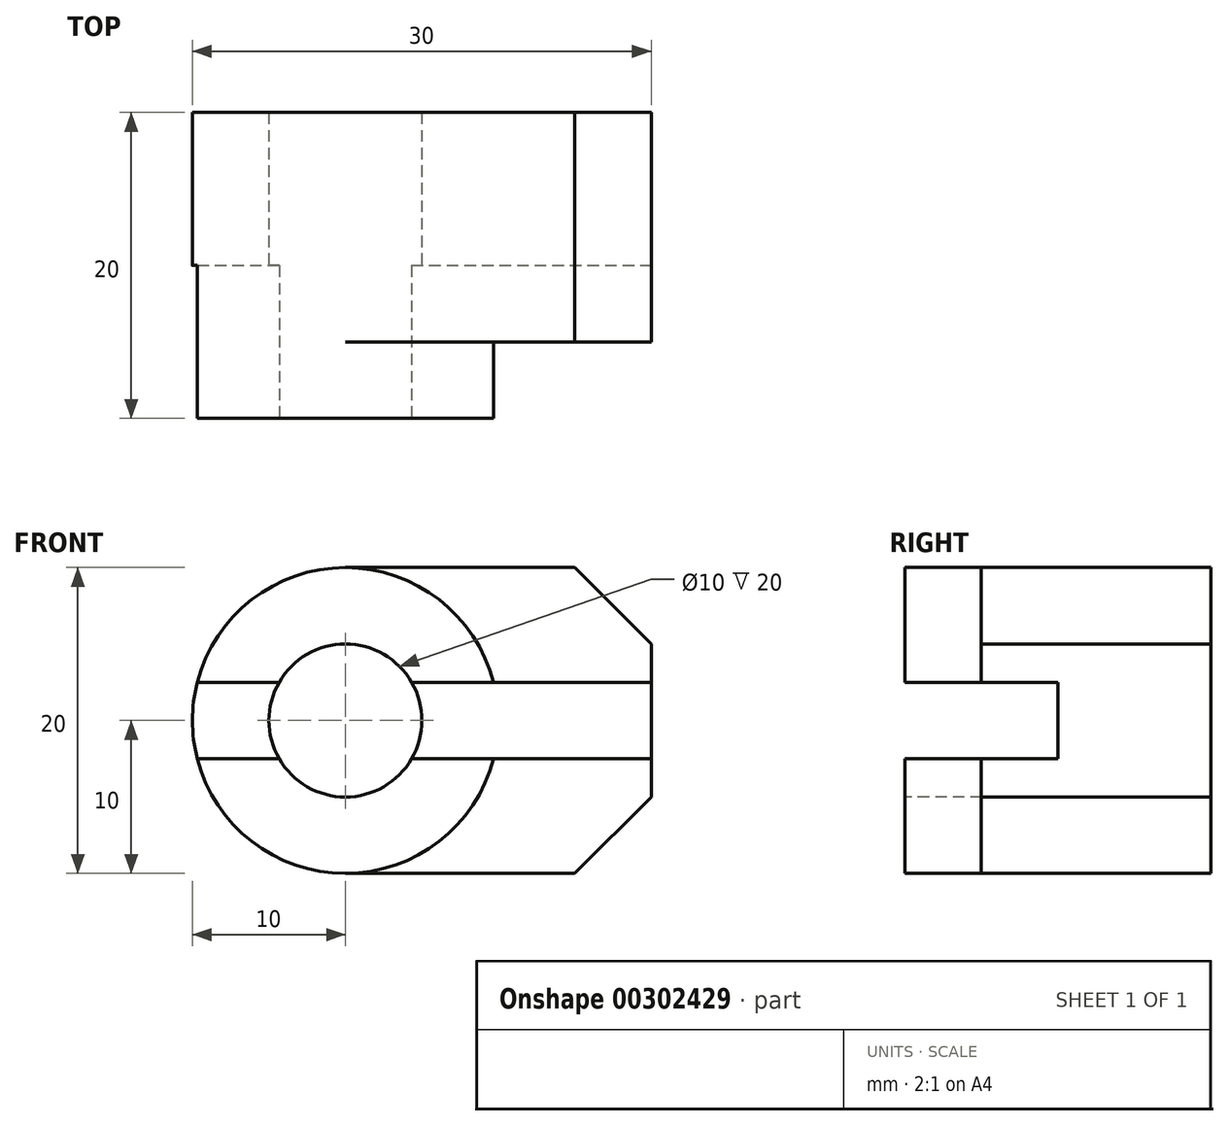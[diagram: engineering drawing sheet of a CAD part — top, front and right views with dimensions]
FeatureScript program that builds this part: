
annotation { "Feature Type Name" : "Feature", "Feature Type Description" : "" }
export const myFeature = defineFeature(function(context is Context, id is Id, definition is map)
    precondition{}
    {
        {
            var Q0;
            Q0=qCreatedBy(makeId("Front.planeOp"),FACE);
            var sketch = newSketch(context, id + "F0", { "sketchPlane" : qUnion([Q0])});
            skCircle(sketch, "E0", {"center": v(0, 0) * mm, "radius": 10 * mm});
            skSolve(sketch);
        }
        {
            var Q0;
            Q0 = qSketchRegion(id + "F0", true);
            extrude(context, id + "F1", {"entities" : qUnion([Q0]), "depth" : 20 * mm});
        }
        {
            var Q0;
            Q0=qCreatedBy(makeId("Front.planeOp"),FACE);
            var sketch = newSketch(context, id + "F2", { "sketchPlane" : qUnion([Q0])});
            skArc(sketch, "E1", {"start": v(10, 0) * mm, "mid": v(7.07, 7.07) * mm, "end": v(0, 10) * mm});
            skLineSegment(sketch, "E2", {"start": v(0, 10) * mm, "end": v(15, 10) * mm});
            skLineSegment(sketch, "E3", {"start": v(15, 10) * mm, "end": v(20, 5) * mm});
            skLineSegment(sketch, "E4", {"start": v(20, 5) * mm, "end": v(20, 0) * mm});
            skLineSegment(sketch, "E5.MirrorCS", {"start": v(0, -10) * mm, "end": v(15, -10) * mm});
            skLineSegment(sketch, "E6.MirrorCS", {"start": v(15, -10) * mm, "end": v(20, -5) * mm});
            skLineSegment(sketch, "E7.MirrorCS", {"start": v(20, -5) * mm, "end": v(20, 0) * mm});
            skArc(sketch, "E8.MirrorCS", {"start": v(10, 0) * mm, "mid": v(7.07, -7.07) * mm, "end": v(0, -10) * mm});
            skSolve(sketch);
        }
        {
            var Q0;
            Q0 = qSketchRegion(id + "F2", true);
            extrude(context, id + "F3", {"entities" : qUnion([Q0]), "operationType" : NewBodyOperationType.ADD, "depth" : 15 * mm});
        }
        {
            var Q0;
            Q0=makeQuery(id+"F1.opExtrude","CAP_FACE",FACE,{"disambiguationData":[OSD([sQuery(id+"F0.wireOp",EDGE,"E0")])],"isStart":false});
            var sketch = newSketch(context, id + "F4", { "sketchPlane" : qUnion([Q0])});
            skCircle(sketch, "E9", {"center": v(0, 0) * mm, "radius": 5 * mm});
            skSolve(sketch);
        }
        {
            var Q0;
            Q0 = qSketchRegion(id + "F4", true);
            extrude(context, id + "F5", {"entities" : qUnion([Q0]), "operationType" : NewBodyOperationType.REMOVE, "endBound" : BoundingType.THROUGH_ALL, "oppositeDirection" : true, "depth" : 25 * mm});
        }
        {
            var Q0;
            Q0=makeQuery(id+"F3.opExtrude","SWEPT_FACE",FACE,{"disambiguationData":[OSD([sQuery(id+"F2.wireOp",EDGE,"E4"),sQuery(id+"F2.wireOp",EDGE,"E7.MirrorCS")])]});
            var sketch = newSketch(context, id + "F6", { "sketchPlane" : qUnion([Q0])});
            skLineSegment(sketch, "E10.bottom", {"start": v(-20, 2.5) * mm, "end": v(-10, 2.5) * mm});
            skLineSegment(sketch, "E10.top", {"start": v(-20, -2.5) * mm, "end": v(-10, -2.5) * mm});
            skLineSegment(sketch, "E10.left", {"start": v(-20, 2.5) * mm, "end": v(-20, -2.5) * mm});
            skLineSegment(sketch, "E10.right", {"start": v(-10, 2.5) * mm, "end": v(-10, -2.5) * mm});
            skSolve(sketch);
        }
        {
            var Q0;
            {var subQ0=sQuery(id+"F6.wireOp",EDGE,"E10.left");Q0=makeQuery(id+"F6.imprint","IMPRINT",FACE,{"disambiguationData":[TD([[makeQuery(id+"F6.imprint","IMPRINT",EDGE,{"derivedFrom":subQ0}),1.0]])]});}
            var Q1;
            {var subQ0=sQuery(id+"F6.wireOp",EDGE,"E10.right");Q1=makeQuery(id+"F6.imprint","IMPRINT",FACE,{"disambiguationData":[TD([[makeQuery(id+"F6.imprint","IMPRINT",EDGE,{"derivedFrom":subQ0}),-1.0]])]});}
            extrude(context, id + "F7", {"entities" : qUnion([Q0, Q1]), "operationType" : NewBodyOperationType.REMOVE, "endBound" : BoundingType.THROUGH_ALL, "oppositeDirection" : true, "depth" : 25 * mm});
        }
    });
